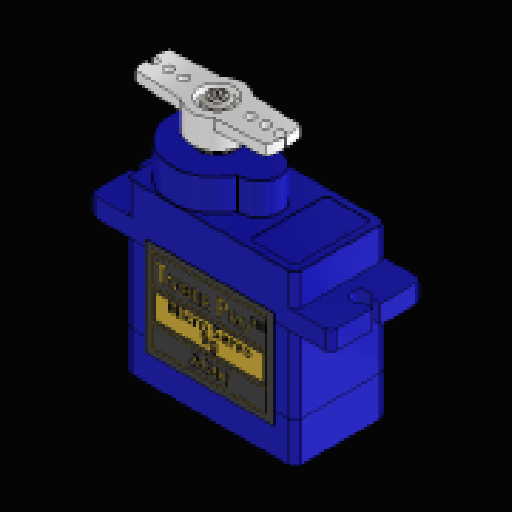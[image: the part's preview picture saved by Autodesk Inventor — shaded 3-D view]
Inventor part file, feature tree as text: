
AUTODESK INVENTOR PART (.ipt)
format: ipt  version: 2023.2 (Build 272271030, 271C)  size: 1,925,632 bytes
history: mixed  units: mm
features: other x18, extrude x1, sketch x1, projected_geometry x1, imported_body x1
ambient origin geometry x8: Origin, YZ Plane, XZ Plane, XY Plane, X Axis, Y Axis, Z Axis, Center Point
bodies: Solid1 (imported_parasolid), Solid2 (imported_parasolid), Solid3 (imported_parasolid), Solid4 (imported_parasolid), Solid5 (imported_parasolid), Solid6 (imported_parasolid), Solid7 (imported_parasolid), Solid8 (imported_parasolid), Solid9 (imported_parasolid), Solid10 (imported_parasolid), Solid11 (imported_parasolid), Solid12 (imported_parasolid), Solid13 (imported_parasolid), Solid14 (imported_parasolid), Solid17 (imported_parasolid)
feature tree (22):
  other  "Plane4"
  other  "Plane4:1"
  other  "Plane4:2"
  extrude  "Extrusion1"  Depth=10.0mm
  sketch  "Sketch2"  dims[d7=18.0mm d8=2.0mm d9=2.0mm d10=10.0mm d11=0.0mm]
  projected_geometry  "Projected Loop1"
  other  "Tower Pro - Micro Servo 9g - SG90.1:1"
  other  "Tower Pro - Micro Servo 9g - SG90.1:2"
  other  "Tower Pro - Micro Servo 9g - SG90.1:3"
  other  "Tower Pro - Micro Servo 9g - SG90.1:4"
  other  "Tower Pro - Micro Servo 9g - SG90.1:5"
  other  "Tower Pro - Micro Servo 9g - SG90.1:6"
  other  "Tower Pro - Micro Servo 9g - SG90.1:7"
  other  "Tower Pro - Micro Servo 9g - SG90.1:8"
  other  "Tower Pro - Micro Servo 9g - SG90.1:9"
  other  "Tower Pro - Micro Servo 9g - SG90.1:10"
  other  "Tower Pro - Micro Servo 9g - SG90.1:11"
  other  "Tower Pro - Micro Servo 9g - SG90.1:12"
  other  "Tower Pro - Micro Servo 9g - SG90.1:13"
  other  "SG90 - Micro Servo 9g - Tower Pro.3:1"
  other  "SG90 - Micro Servo 9g - Tower Pro.6:1"
  imported_body  NMx_Import_Brep_tag  [imported B-rep: ~76 faces, bbox_mm=[18.75, 10.3, 12.4]]
